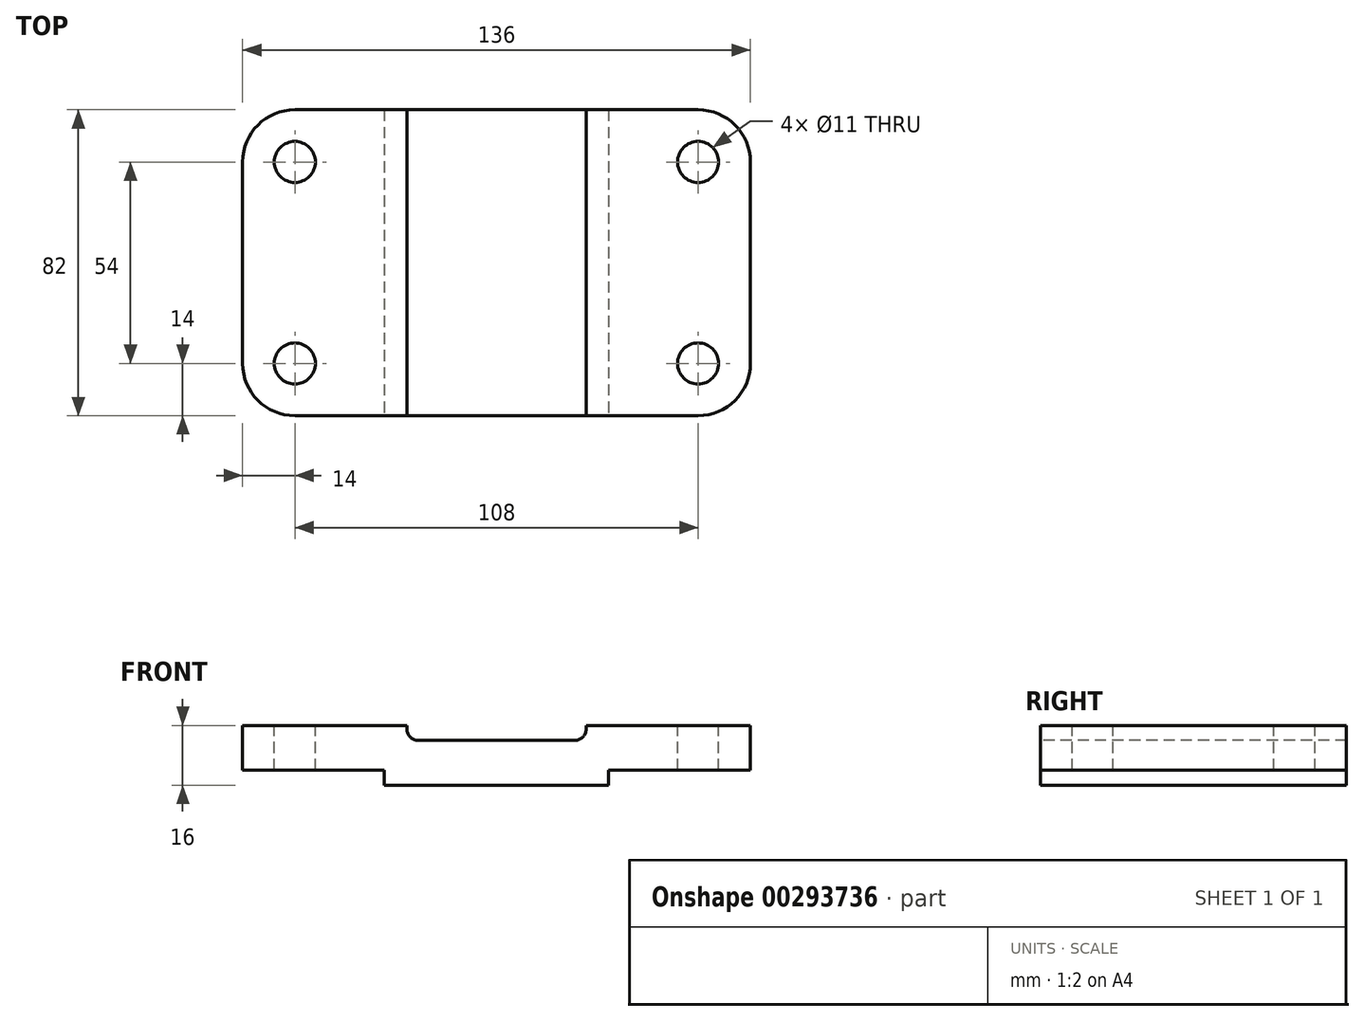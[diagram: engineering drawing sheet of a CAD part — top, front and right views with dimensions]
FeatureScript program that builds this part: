
annotation { "Feature Type Name" : "Feature", "Feature Type Description" : "" }
export const myFeature = defineFeature(function(context is Context, id is Id, definition is map)
    precondition{}
    {
        {
            var Q0;
            Q0=qCreatedBy(makeId("Front.planeOp"),FACE);
            var sketch = newSketch(context, id + "F0", { "sketchPlane" : qUnion([Q0])});
            skLineSegment(sketch, "E0", {"start": v(0, 0) * mm, "end": v(44, 0) * mm});
            skLineSegment(sketch, "E1", {"start": v(44, 0) * mm, "end": v(44, -1) * mm});
            skLineSegment(sketch, "E2", {"start": v(47, -4) * mm, "end": v(89, -4) * mm});
            skLineSegment(sketch, "E3", {"start": v(92, -1) * mm, "end": v(92, 0) * mm});
            skLineSegment(sketch, "E4", {"start": v(92, 0) * mm, "end": v(136, 0) * mm});
            skLineSegment(sketch, "E5", {"start": v(136, 0) * mm, "end": v(136, -12) * mm});
            skLineSegment(sketch, "E6", {"start": v(136, -12) * mm, "end": v(98, -12) * mm});
            skLineSegment(sketch, "E7", {"start": v(98, -12) * mm, "end": v(98, -16) * mm});
            skLineSegment(sketch, "E8", {"start": v(98, -16) * mm, "end": v(38, -16) * mm});
            skLineSegment(sketch, "E9", {"start": v(38, -16) * mm, "end": v(38, -12) * mm});
            skLineSegment(sketch, "E10", {"start": v(38, -12) * mm, "end": v(0, -12) * mm});
            skLineSegment(sketch, "E11", {"start": v(0, -12) * mm, "end": v(0, 0) * mm});
            skPoint(sketch, "E12.visualSharp", {"position": v(44, -4) * mm});
            skArc(sketch, "E12.filletArc", {"start": v(44, -1) * mm, "mid": v(44.88, -3.12) * mm, "end": v(47, -4) * mm});
            skPoint(sketch, "E13.visualSharp", {"position": v(92, -4) * mm});
            skArc(sketch, "E13.filletArc", {"start": v(89, -4) * mm, "mid": v(91.12, -3.12) * mm, "end": v(92, -1) * mm});
            skSolve(sketch);
        }
        {
            var Q0;
            Q0 = qSketchRegion(id + "F0", true);
            extrude(context, id + "F1", {"entities" : qUnion([Q0]), "oppositeDirection" : true, "depth" : 82 * mm});
        }
        {
            var Q0;
            Q0=makeQuery(id+"F1.opExtrude","CAP_EDGE",EDGE,{"disambiguationData":[OSD([sQuery(id+"F0.wireOp",EDGE,"E11")])],"isStart":false});
            var Q1;
            Q1=makeQuery(id+"F1.opExtrude","CAP_EDGE",EDGE,{"disambiguationData":[OSD([sQuery(id+"F0.wireOp",EDGE,"E11")])],"isStart":true});
            var Q2;
            Q2=makeQuery(id+"F1.opExtrude","CAP_EDGE",EDGE,{"disambiguationData":[OSD([sQuery(id+"F0.wireOp",EDGE,"E5")])],"isStart":true});
            var Q3;
            Q3=makeQuery(id+"F1.opExtrude","CAP_EDGE",EDGE,{"disambiguationData":[OSD([sQuery(id+"F0.wireOp",EDGE,"E5")])],"isStart":false});
            fillet(context, id + "F2", {"entities" : qUnion([Q0, Q1, Q2, Q3]), "radius" : 14 * mm, "tangentPropagation" : true, "allowEdgeOverflow" : false});
        }
        {
            var Q0;
            Q0=makeQuery(id+"F1.opExtrude","SWEPT_FACE",FACE,{"disambiguationData":[OSD([sQuery(id+"F0.wireOp",EDGE,"E0")])]});
            var sketch = newSketch(context, id + "F3", { "sketchPlane" : qUnion([Q0])});
            skLineSegment(sketch, "E14.0.0", {"start": v(0, 68) * mm, "end": v(0, 14) * mm});
            skArc(sketch, "E14.0.1", {"start": v(0, 14) * mm, "mid": v(4.1, 4.1) * mm, "end": v(14, 0) * mm});
            skLineSegment(sketch, "E14.0.2", {"start": v(14, 0) * mm, "end": v(44, 0) * mm});
            skLineSegment(sketch, "E14.0.3", {"start": v(44, 0) * mm, "end": v(44, 82) * mm});
            skLineSegment(sketch, "E14.0.4", {"start": v(44, 82) * mm, "end": v(14, 82) * mm});
            skArc(sketch, "E14.0.5", {"start": v(14, 82) * mm, "mid": v(4.1, 77.9) * mm, "end": v(0, 68) * mm});
            skCircle(sketch, "E15", {"center": v(14, 68) * mm, "radius": 5.5 * mm});
            skCircle(sketch, "E16.0.1.0", {"center": v(14, 14) * mm, "radius": 5.5 * mm});
            skCircle(sketch, "E16.1.0.0", {"center": v(122, 68) * mm, "radius": 5.5 * mm});
            skCircle(sketch, "E16.1.1.0", {"center": v(122, 14) * mm, "radius": 5.5 * mm});
            skLineSegment(sketch, "E16.direction1", {"start": v(14, 68) * mm, "end": v(122, 68) * mm, "construction": true});
            skLineSegment(sketch, "E16.direction2", {"start": v(14, 68) * mm, "end": v(14, 14) * mm, "construction": true});
            skSolve(sketch);
        }
        {
            var Q0;
            Q0=makeQuery(id+"F3.imprint","IMPRINT",FACE,{"disambiguationData":[TD([[makeQuery(id+"F3.imprint","IMPRINT",EDGE,{"derivedFrom":sQuery(id+"F3.wireOp",EDGE,"E15")}),1.0]])]});
            var Q1;
            Q1=makeQuery(id+"F3.imprint","IMPRINT",FACE,{"disambiguationData":[TD([[makeQuery(id+"F3.imprint","IMPRINT",EDGE,{"derivedFrom":sQuery(id+"F3.wireOp",EDGE,"E16.0.1.0")}),1.0]])]});
            var Q2;
            Q2=makeQuery(id+"F3.imprint","IMPRINT",FACE,{"disambiguationData":[TD([[makeQuery(id+"F3.imprint","IMPRINT",EDGE,{"derivedFrom":sQuery(id+"F3.wireOp",EDGE,"E16.1.1.0")}),1.0]])]});
            var Q3;
            Q3=makeQuery(id+"F3.imprint","IMPRINT",FACE,{"disambiguationData":[TD([[makeQuery(id+"F3.imprint","IMPRINT",EDGE,{"derivedFrom":sQuery(id+"F3.wireOp",EDGE,"E16.1.0.0")}),1.0]])]});
            extrude(context, id + "F4", {"entities" : qUnion([Q0, Q1, Q2, Q3]), "operationType" : NewBodyOperationType.REMOVE, "oppositeDirection" : true, "depth" : 25 * mm});
        }
    });
